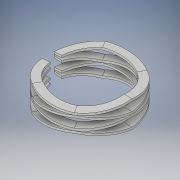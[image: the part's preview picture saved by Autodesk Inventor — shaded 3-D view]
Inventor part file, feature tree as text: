
AUTODESK INVENTOR PART (.ipt)
format: ipt  version: 2018 (Build 220112000, 112)  size: 340,992 bytes
history: native  units: in
note: dims shown in document units (in); Inventor stores cm internally (conversion verified against a paired STEP export)
features: sketch x7, projected_geometry x6, extrude x5, plane x2, pattern_circular x2, mirror x1
ambient origin geometry x8: Origin, YZ Plane, XZ Plane, XY Plane, X Axis, Y Axis, Z Axis, Center Point
bodies: Solid1 (feature_tree)
feature tree (23):
  extrude  "Extrusion1"  Depth=1.73in
  sketch  "Sketch3"  dims[d2=0.552in d3=0.0in d7=2.3622in d9=360.0deg]
  sketch  "Sketch5"  dims[d22=0.5767in d23=0.5765in d24=0.5768in d25=0.045in d26=0.045in d27=0.09in d28=0.045in d29=0.045in d30=0.09in d31=0.045in d32=0.09in]
  plane  "Work Plane1"
  sketch  "Sketch11"  dims[d42=0.002in]
  plane  "Work Plane2"
  extrude  "Extrusion9"  Depth=2.3622in TaperAngle=360.0deg
  mirror  "Mirror6"
  pattern_circular  "Circular Pattern1"  Count=3 Angle=360.0deg
  extrude  "Extrusion10"  Depth=1.0in TaperAngle=0.0deg
  extrude  "Extrusion11"  Depth=1.1811in TaperAngle=360.0deg
  pattern_circular  "Circular Pattern2"  [2 undecoded]
  extrude  "Extrusion12"  Depth=0.1225in
  sketch  "Sketch1"  dims[d0=1.41in d1=1.73in]
  projected_geometry  "Projected Loop10"
  sketch  "Sketch13"  dims[d45=1.1025in]
  projected_geometry  "Projected Loop12"
  sketch  "Sketch14"  dims[d51=1.0in d52=0.0in d53=1.1811in d54=360.0deg]
  projected_geometry  "Projected Loop13"
  projected_geometry  "Projected Loop14"
  projected_geometry  "Projected Loop15"
  projected_geometry  "Projected Loop16"
  sketch  "Sketch15"  dims[d56=1.0in d57=0.0in d58=1.0in d59=0.0in d60=1.1811in d61=360.0deg d63=0.1225in d64=0.1225in d65=1.0in d66=0.0in]
note: 2 required parameter values undecoded (feature->parameter linkage not recoverable at this tier; creation-order binding heuristic only, values carry confidence <= 0.55)
